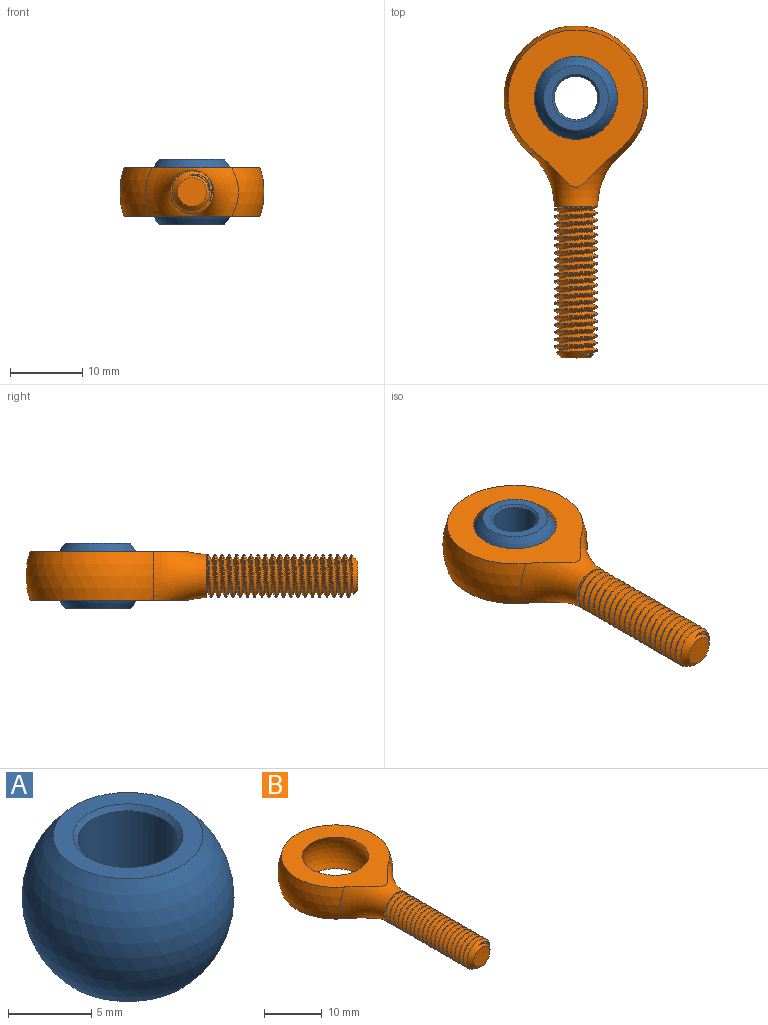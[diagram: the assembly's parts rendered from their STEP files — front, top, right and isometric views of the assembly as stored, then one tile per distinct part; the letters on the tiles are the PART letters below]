
ASSEMBLY  parts=2 mates=1
PART A: 6 faces, bbox 12.7x12.7x9 mm
  f0: cone r=3mm half-angle=45deg, axis (0,0,1), area 8.4mm2, adj f2,f4
  f1: cone r=3.3mm half-angle=45deg, axis (0,0,-1), area 8.4mm2, adj f2,f5
  f2: cylinder r=3mm len=8.4mm, axis (0,0,1), area 158.3mm2, adj f0,f1
  f3: sphere r=6.35mm, area 359.1mm2, adj f4,f5
  f4: plane 8.96x8.96mm, normal (0,0,1), area 28.8mm2, adj f0,f3
  f5: plane 8.96x8.96mm, normal (0,0,-1), area 28.8mm2, adj f1,f3
PART B: 12 faces, bbox 27.6x46.5x27.6 mm
  f0: sphere r=6.67mm, area 282.8mm2, adj f10,f11
  f1: sphere r=10mm, area 337.8mm2, adj f2,f10,f11
  f2: torus R=12.57mm, axis (0,-1,0), area 141.8mm2, adj f1,f4,f9,f10,f11
  f3: cone r=3mm half-angle=45deg, axis (0,1,0), area 14.3mm2, adj f4,f5,f6,f7,f8
  f4: cylinder r=3mm len=20mm, axis (0,1,0), area 47.1mm2, adj f2,f3,f7,f8
  f5: plane 4x4mm, normal (0,-1,0), area 12.6mm2, adj f3
  f6: bspline ~20.9x4.7mm, area 38.2mm2, adj f3,f7,f8,f9
  f7: bspline ~21.25x6mm, area 256.7mm2, adj f3,f4,f6,f9
  f8: bspline ~21.5x6mm, area 256.4mm2, adj f3,f4,f6,f9
  f9: plane 6.38x6.38mm, normal (0,-1,0), area 5.6mm2, adj f2,f6,f7,f8
  f10: plane 21.77x18.83mm, normal (0,0,1), area 188mm2, adj f0,f1,f2
  f11: plane 21.77x18.83mm, normal (0,0,-1), area 188mm2, adj f0,f1,f2
PLACE A at identity
PLACE B at identity
MATE ball B.f0 <-> A.f0  axis (0,0,1) through (0,15,0)mm
